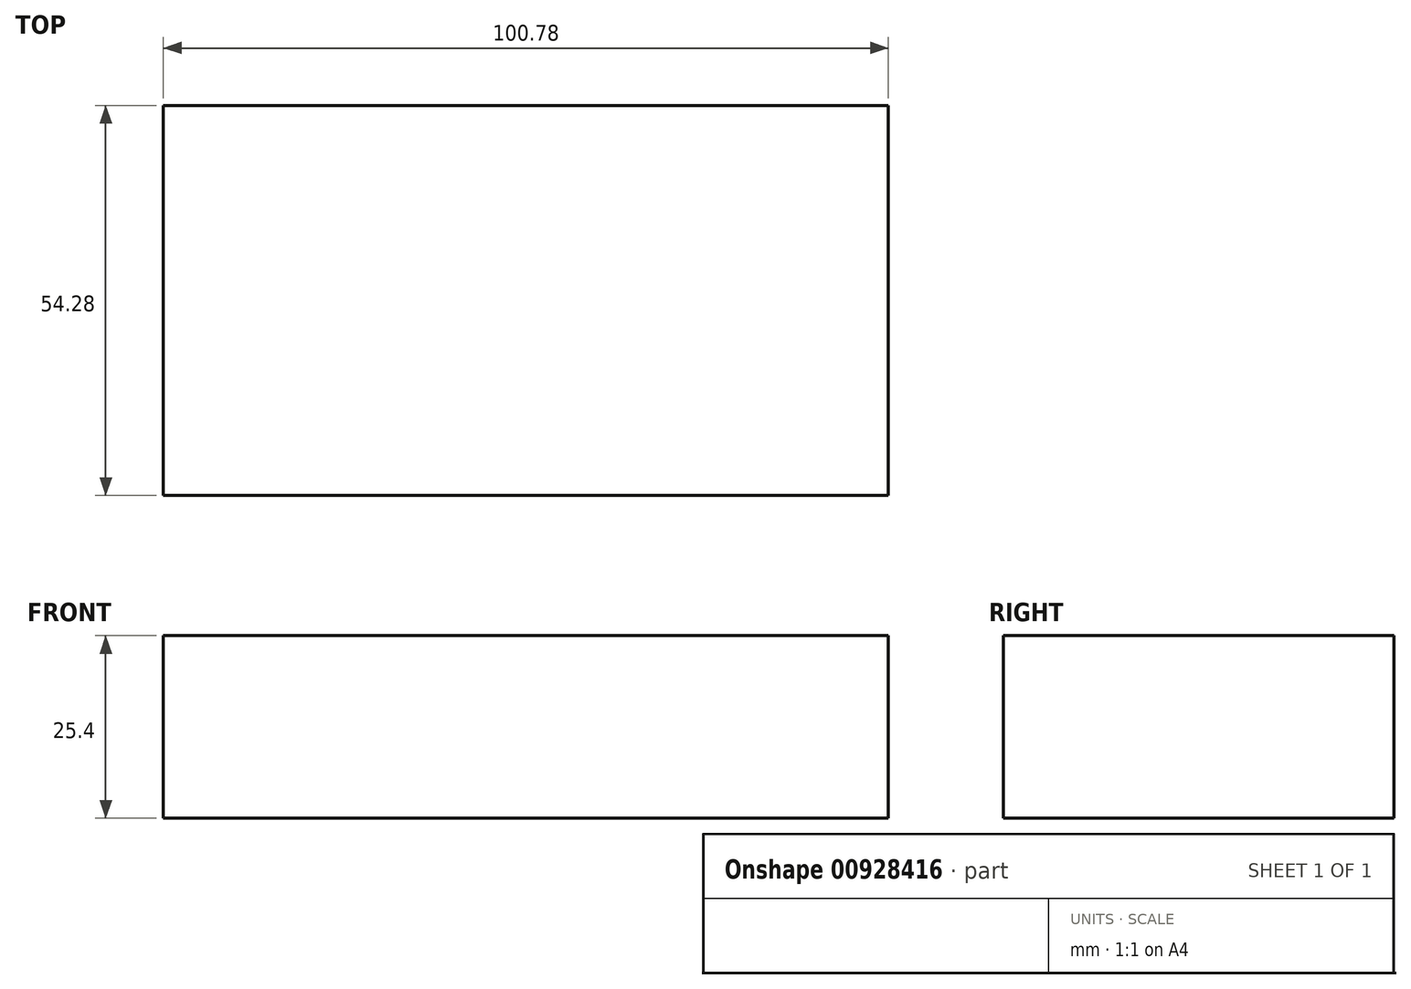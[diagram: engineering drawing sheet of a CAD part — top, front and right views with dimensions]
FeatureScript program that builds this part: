
annotation { "Feature Type Name" : "Feature", "Feature Type Description" : "" }
export const myFeature = defineFeature(function(context is Context, id is Id, definition is map)
    precondition{}
    {
        {
            var Q0;
            Q0=qCreatedBy(makeId("Top.planeOp"),FACE);
            var sketch = newSketch(context, id + "F0", { "sketchPlane" : qUnion([Q0])});
            skLineSegment(sketch, "E0.bottom", {"start": v(0, 0) * mm, "end": v(-100.78, 0) * mm});
            skLineSegment(sketch, "E0.top", {"start": v(0, 54.28) * mm, "end": v(-100.78, 54.28) * mm});
            skLineSegment(sketch, "E0.left", {"start": v(0, 0) * mm, "end": v(0, 54.28) * mm});
            skLineSegment(sketch, "E0.right", {"start": v(-100.78, 0) * mm, "end": v(-100.78, 54.28) * mm});
            skSolve(sketch);
        }
        {
            var Q0;
            Q0 = qSketchRegion(id + "F0", true);
            extrude(context, id + "F1", {"entities" : qUnion([Q0]), "depth" : 25.4 * mm, "offsetDistance" : 25.4 * mm});
        }
    });
